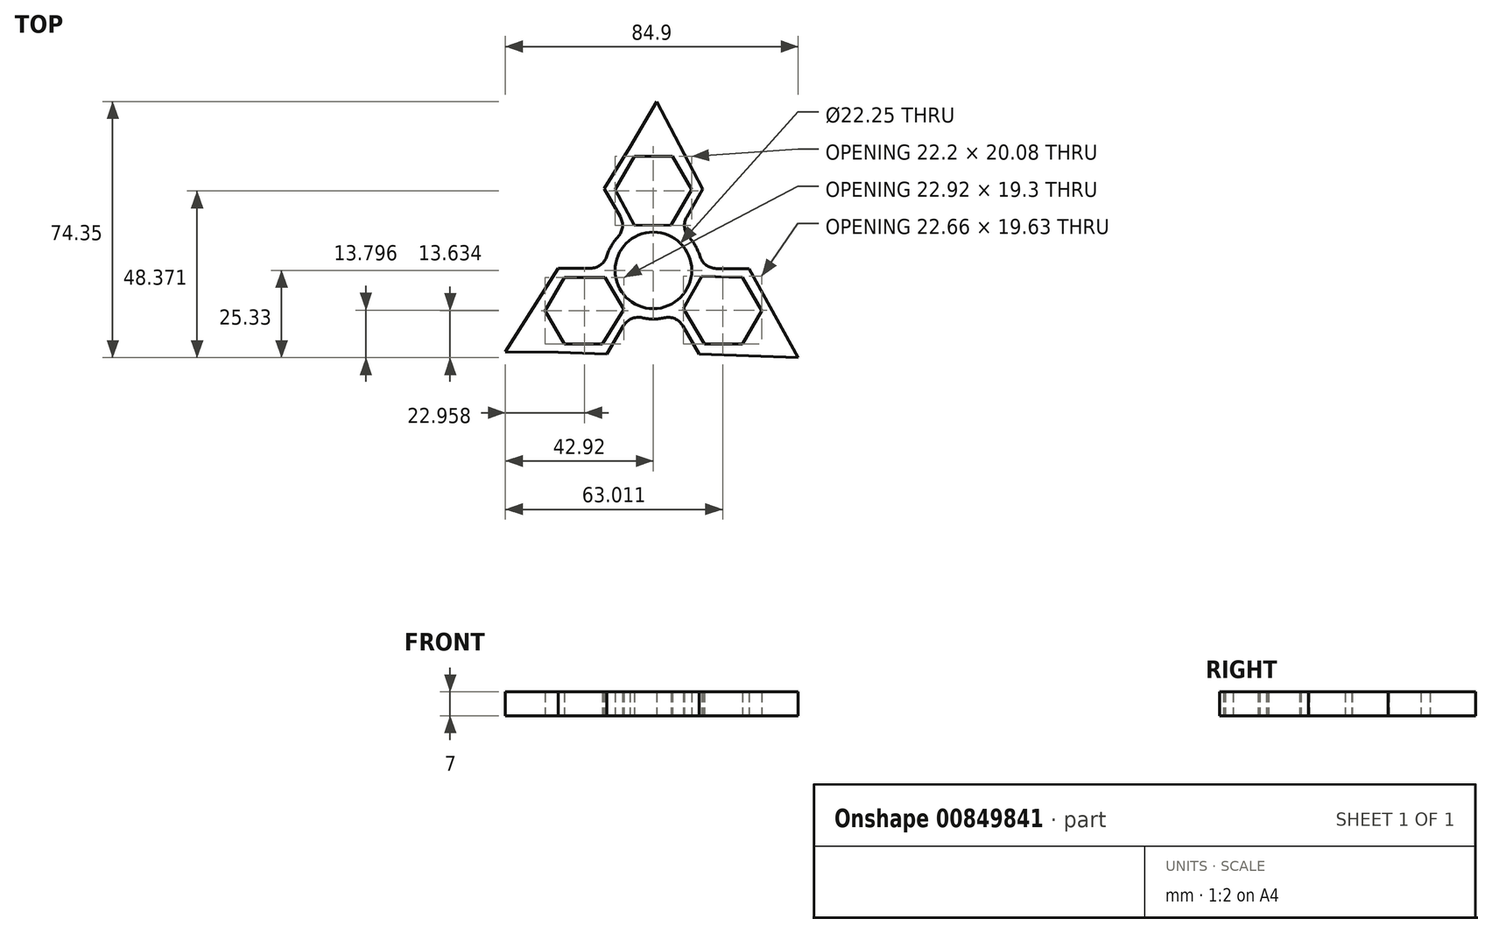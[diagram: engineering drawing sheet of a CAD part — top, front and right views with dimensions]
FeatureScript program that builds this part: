
annotation { "Feature Type Name" : "Feature", "Feature Type Description" : "" }
export const myFeature = defineFeature(function(context is Context, id is Id, definition is map)
    precondition{}
    {
        {
            var Q0;
            Q0=qCreatedBy(makeId("Top.planeOp"),FACE);
            var sketch = newSketch(context, id + "F0", { "sketchPlane" : qUnion([Q0])});
            skCircle(sketch, "E0", {"center": v(0, 0) * mm, "radius": 11.12 * mm});
            skLineSegment(sketch, "E1.0", {"start": v(0.94, 49.02) * mm, "end": v(-6.8, 35.8) * mm});
            skLineSegment(sketch, "E1.1", {"start": v(0.94, 49.02) * mm, "end": v(14.35, 23.6) * mm});
            skLineSegment(sketch, "E1.2", {"start": v(14.35, 23.6) * mm, "end": v(9.68, 15.51) * mm});
            skLineSegment(sketch, "E1.4", {"start": v(-9.6, 15.55) * mm, "end": v(-14.26, 23.76) * mm});
            skLineSegment(sketch, "E1.5", {"start": v(-6.8, 35.8) * mm, "end": v(-14.26, 23.76) * mm});
            skLineSegment(sketch, "E2.0", {"start": v(-5.55, 33.08) * mm, "end": v(5.55, 33.08) * mm});
            skLineSegment(sketch, "E2.1", {"start": v(5.55, 33.08) * mm, "end": v(11.1, 23.46) * mm});
            skLineSegment(sketch, "E2.2", {"start": v(11.1, 23.46) * mm, "end": v(5.22, 13.13) * mm});
            skLineSegment(sketch, "E2.4", {"start": v(-5.52, 13) * mm, "end": v(-11.1, 23.46) * mm});
            skLineSegment(sketch, "E2.5", {"start": v(-11.1, 23.46) * mm, "end": v(-5.55, 33.08) * mm});
            skArc(sketch, "E3.0", {"start": v(-10.3, 9.66) * mm, "mid": v(-12.21, 7.1) * mm, "end": v(-13.5, 4.16) * mm});
            skLineSegment(sketch, "E4.1.0", {"start": v(-25.87, -2.12) * mm, "end": v(-13.98, -2.05) * mm});
            skLineSegment(sketch, "E4.1.1", {"start": v(-27.61, 0.63) * mm, "end": v(-18.28, 0.63) * mm});
            skLineSegment(sketch, "E4.1.2", {"start": v(-25.87, -21.35) * mm, "end": v(-31.42, -11.73) * mm});
            skLineSegment(sketch, "E4.1.3", {"start": v(-42.92, -23.7) * mm, "end": v(-27.61, 0.63) * mm});
            skLineSegment(sketch, "E4.1.4", {"start": v(-31.42, -11.73) * mm, "end": v(-25.87, -2.12) * mm});
            skLineSegment(sketch, "E4.1.5", {"start": v(-8.5, -11.28) * mm, "end": v(-14.77, -21.35) * mm});
            skLineSegment(sketch, "E4.1.6", {"start": v(-8.67, -16.09) * mm, "end": v(-13.45, -24.23) * mm});
            skLineSegment(sketch, "E4.1.7", {"start": v(-14.77, -21.35) * mm, "end": v(-25.87, -21.35) * mm});
            skLineSegment(sketch, "E4.1.8", {"start": v(-27.6, -23.79) * mm, "end": v(-13.45, -24.23) * mm});
            skLineSegment(sketch, "E4.1.9", {"start": v(-42.92, -23.7) * mm, "end": v(-27.6, -23.79) * mm});
            skLineSegment(sketch, "E4.2.0", {"start": v(14.77, -21.35) * mm, "end": v(8.76, -11.08) * mm});
            skLineSegment(sketch, "E4.2.1", {"start": v(13.26, -24.23) * mm, "end": v(8.6, -16.14) * mm});
            skLineSegment(sketch, "E4.2.2", {"start": v(31.42, -11.73) * mm, "end": v(25.87, -21.35) * mm});
            skLineSegment(sketch, "E4.2.3", {"start": v(41.98, -25.33) * mm, "end": v(13.26, -24.23) * mm});
            skLineSegment(sketch, "E4.2.4", {"start": v(25.87, -21.35) * mm, "end": v(14.77, -21.35) * mm});
            skLineSegment(sketch, "E4.2.5", {"start": v(14.02, -1.72) * mm, "end": v(25.87, -2.12) * mm});
            skLineSegment(sketch, "E4.2.6", {"start": v(18.27, 0.54) * mm, "end": v(27.7, 0.47) * mm});
            skLineSegment(sketch, "E4.2.7", {"start": v(25.87, -2.12) * mm, "end": v(31.42, -11.73) * mm});
            skArc(sketch, "E5.trimOffspring", {"start": v(-3.22, -13.75) * mm, "mid": v(-0.04, -14.12) * mm, "end": v(3.15, -13.77) * mm});
            skArc(sketch, "E6.trimOffspring", {"start": v(13.52, 4.1) * mm, "mid": v(12.25, 7.03) * mm, "end": v(10.35, 9.61) * mm});
            skPoint(sketch, "E7.newPointA", {"position": v(13.85, 0.57) * mm});
            skArc(sketch, "E7.filletArc", {"start": v(13.52, 4.1) * mm, "mid": v(15.31, 1.53) * mm, "end": v(18.27, 0.54) * mm});
            skPoint(sketch, "E8.newPointA", {"position": v(7.18, 11.17) * mm});
            skArc(sketch, "E8.filletArc", {"start": v(9.68, 15.51) * mm, "mid": v(9.05, 12.45) * mm, "end": v(10.35, 9.61) * mm});
            skPoint(sketch, "E9.newPointB", {"position": v(-13.26, 0.63) * mm});
            skArc(sketch, "E9.filletArc", {"start": v(-18.28, 0.63) * mm, "mid": v(-15.3, 1.6) * mm, "end": v(-13.5, 4.16) * mm});
            skPoint(sketch, "E10.newPointB", {"position": v(-7.42, 11.7) * mm});
            skArc(sketch, "E10.filletArc", {"start": v(-10.3, 9.66) * mm, "mid": v(-8.98, 12.5) * mm, "end": v(-9.6, 15.55) * mm});
            skPoint(sketch, "E11.newPointA", {"position": v(-6.43, -12.28) * mm});
            skArc(sketch, "E11.filletArc", {"start": v(-3.22, -13.75) * mm, "mid": v(-6.33, -14.03) * mm, "end": v(-8.67, -16.09) * mm});
            skPoint(sketch, "E12.newPointB", {"position": v(6.09, -11.8) * mm});
            skArc(sketch, "E12.filletArc", {"start": v(8.6, -16.14) * mm, "mid": v(6.26, -14.06) * mm, "end": v(3.15, -13.77) * mm});
            skPoint(sketch, "E13.visualSharp", {"position": v(34.4, -12) * mm});
            skLineSegment(sketch, "E13.filletArc", {"start": v(21.63, 11.79) * mm, "end": v(21.63, 11.79) * mm});
            skLineSegment(sketch, "E14", {"start": v(8.76, -11.08) * mm, "end": v(14.02, -1.72) * mm});
            skLineSegment(sketch, "E15", {"start": v(-8.5, -11.28) * mm, "end": v(-13.98, -2.05) * mm});
            skLineSegment(sketch, "E16", {"start": v(-5.52, 13) * mm, "end": v(5.22, 13.13) * mm});
            skLineSegment(sketch, "E17", {"start": v(41.98, -25.33) * mm, "end": v(27.7, 0.47) * mm});
            skSolve(sketch);
        }
        {
            var Q0;
            Q0 = qSketchRegion(id + "F0", true);
            extrude(context, id + "F1", {"entities" : qUnion([Q0]), "depth" : 7 * mm, "offsetDistance" : 25 * mm});
        }
        {
            var Q0;
            Q0 = qSketchRegion(id + "F0", true);
            extrude(context, id + "F2", {"entities" : qUnion([Q0]), "operationType" : NewBodyOperationType.ADD, "depth" : 7 * mm, "offsetDistance" : 25 * mm});
        }
        {
            var Q0;
            Q0 = qSketchRegion(id + "F0", true);
            extrude(context, id + "F3", {"entities" : qUnion([Q0]), "operationType" : NewBodyOperationType.ADD, "depth" : 7 * mm, "offsetDistance" : 25 * mm});
        }
    });
